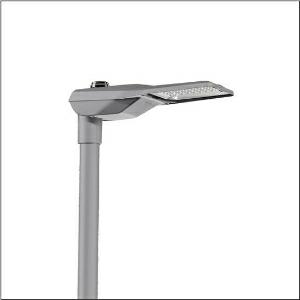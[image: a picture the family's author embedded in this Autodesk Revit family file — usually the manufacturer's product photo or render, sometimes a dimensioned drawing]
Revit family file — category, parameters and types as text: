
# Revit family: streetlight_sl_21_mini___st0_8a_5xe6c47n08hb_c463
name_source: partatom
category: Lighting Fixtures
units: mm (PartAtom-declared; Revit-internal decimal feet)

## family parameters
Cut with Voids When Loaded = No
Host = Face
Light Source = No
Part Type = Normal
Room Calculation Point = No
Round Connector Dimension = Use Diameter
Shared = No

## types (1)
- --- (1 x LED, 9430 lm, 66 W, 4000K)
    Apparent Load = 66 VA
    CIE Flux Codes = 38 75 97 100 100
    Color Rendering = 70
    Color Temperature = 4000K
    Default Elevation = 1800 mm
    Description = Streetlight SL 21 mini, mast luminaire, primary light control with lens, of PMMA, primary optical cover: cover, of toughened safety glass, transparent, light distribution: ST0.8a, light emission: direct distribution, primary light characteristic: asymmetric, installation type: side-entry, LED, 3G 1.5mm², High Power LED, rated luminous flux: 9.430lm, luminous efficacy: 143lm/W, light colour: 740, colour temperature: 4000K, control gear: NEMA (7pin), control: overheat protection, pre-setting: linear dimming characteristic, constant luminous flux control, time-dependent luminous flux control, flexible luminous flux parameterisation, mains connection: 230..240V, AC, 50/60Hz, connection cable pre-assembled, cable length: 8,5m, wiring characteristics: H07RN-F, start of lifetime: 66W, end of service life: 69W, reduction: 30W, luminaire housing, of diecast aluminium (EN AC-44300), powder-coated, SITECO metallic grey (DB 702S), corrosivity category C5 high according to DIN EN ISO 12944, multi-level sealing system, sealing non-destructively replaceable, inclination adjustable: 0°, 5°, 10°, 15°, length: 628mm, width: 235mm, height: 110mm, spigot size: 42mm (side-entry), mounting height: 4..8m, protection rating (complete): IP66, insulation class (complete): insulation class I (protective earthing), certification: CE, ENEC, ENEC+, VDE, impact resistance: IK10, permissible operating ambient temperature for outdoor applications: -40..+50°C, standard-compliant lighting for roads and squares, packaging unit: 1 piece

Light Distribution: ST0.8a
    Height = 110 mm
    Lamp = 1 x LED
    Lamp Light Flux = 9430 lm
    Lamp Power = 66 W
    Lamp count = 1
    Length = 625 mm
    Luminous efficacy = 143 lm/W
    Manufacturer = Siteco
    ModVariant = No
    Model = 5XE6C47N08HB
    Number of Poles = 1
    OnlyDefault = Yes
    Power Factor = 1
    Product Name = Streetlight SL 21 mini | ST0.8a
    Product group = mast luminaire | pylon top
    ProductGroupID = 6100
    Protection Class = Protection class I
    Protection Degree = IP 66
    RLX_Detail_Level = 1
    RLX_Emergency_Light_Flux = 0 lm
    RLX_Emergency_Type = 0
    RLX_Emergency_Type_DB = No
    RlxData = <blob elided: 26169 chars, md5=2c2043de>
    Socket = socket
    Standby Power = 0 W
    System Light Flux = 9430 lm
    System Power = 66 W
    Type Comments = factory setting: luminous flux: 100 % | dim-lin: 254 | 670 mA
    Type Image = l_1294379.jpg
    URL = http://relux.com
    VarID = @adj_133643
    Voltage = 0 V
    Weight = 0.00 kg
    Width = 234 mm

## geometry (parser evidence)
native form markers: Blend x4, Sweep x9
no freeform markers — native parametric forms only
